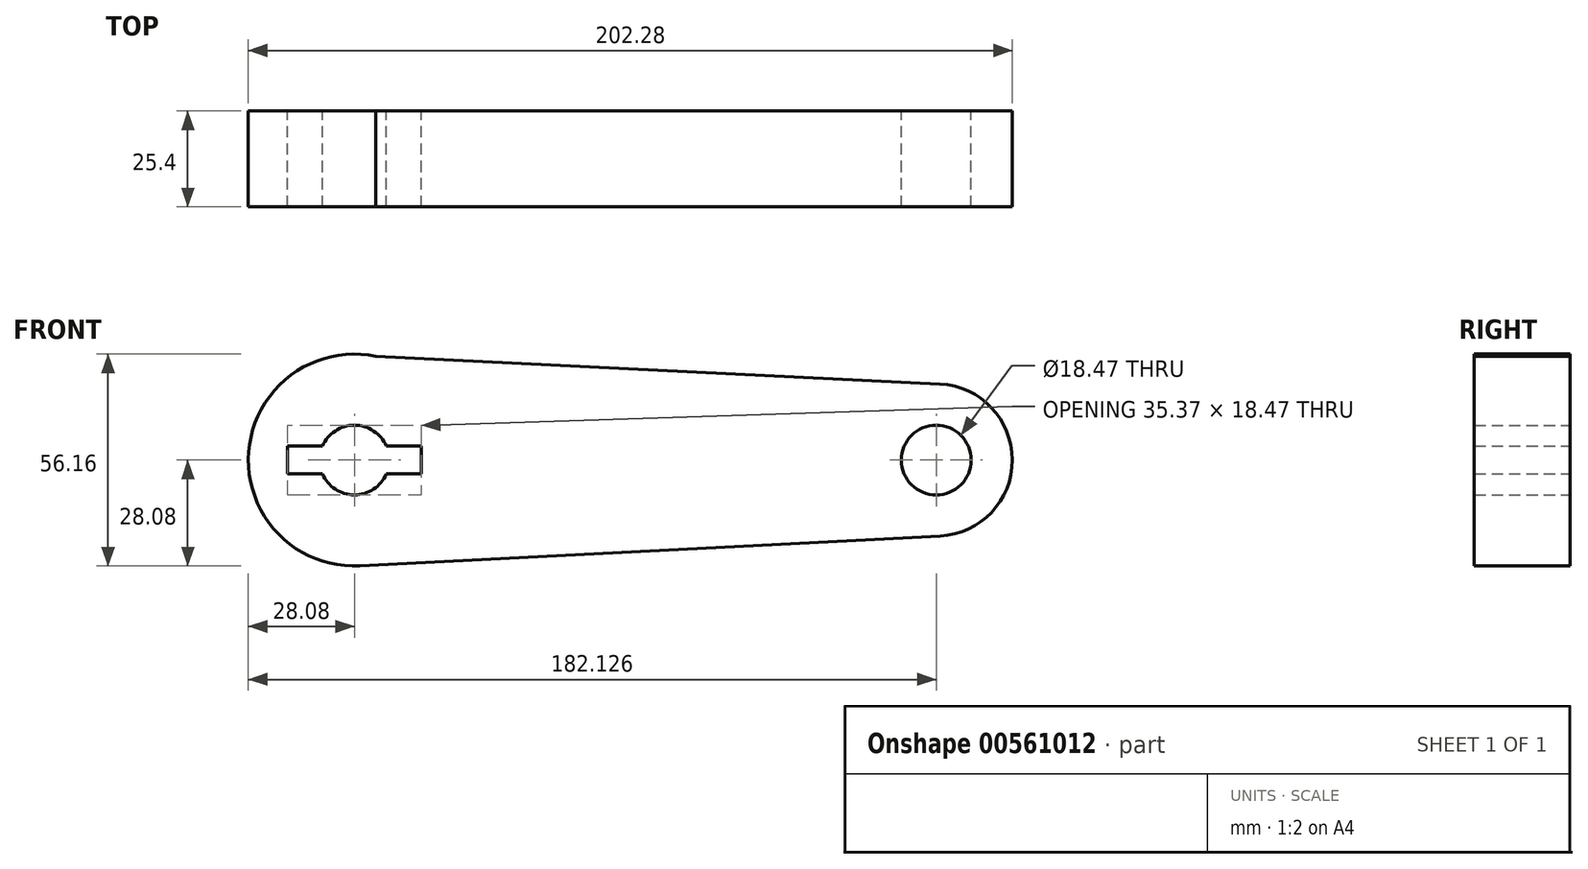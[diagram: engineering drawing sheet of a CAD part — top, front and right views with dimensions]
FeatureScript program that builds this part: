
annotation { "Feature Type Name" : "Feature", "Feature Type Description" : "" }
export const myFeature = defineFeature(function(context is Context, id is Id, definition is map)
    precondition{}
    {
        {
            var Q0;
            Q0=qCreatedBy(makeId("Front.planeOp"),FACE);
            var sketch = newSketch(context, id + "F0", { "sketchPlane" : qUnion([Q0])});
            skCircle(sketch, "E0", {"center": v(0, 0) * mm, "radius": 28.08 * mm});
            skCircle(sketch, "E1", {"center": v(154.05, 0) * mm, "radius": 20.15 * mm});
            skLineSegment(sketch, "E2", {"start": v(5.7, 27.49) * mm, "end": v(155.04, 20.13) * mm});
            skLineSegment(sketch, "E3", {"start": v(1.44, -28.04) * mm, "end": v(155.08, -20.13) * mm});
            skCircle(sketch, "E4", {"center": v(0, 0) * mm, "radius": 9.24 * mm});
            skCircle(sketch, "E5", {"center": v(154.05, 0) * mm, "radius": 9.24 * mm});
            skLineSegment(sketch, "E6.bottom", {"start": v(17.69, 3.68) * mm, "end": v(-17.69, 3.68) * mm});
            skLineSegment(sketch, "E6.top", {"start": v(17.69, -3.68) * mm, "end": v(-17.69, -3.68) * mm});
            skLineSegment(sketch, "E6.left", {"start": v(17.69, 3.68) * mm, "end": v(17.69, -3.68) * mm});
            skLineSegment(sketch, "E6.right", {"start": v(-17.69, 3.68) * mm, "end": v(-17.69, -3.68) * mm});
            skSolve(sketch);
        }
        {
            var Q0;
            Q0 = qSketchRegion(id + "F0", true);
            extrude(context, id + "F1", {"entities" : qUnion([Q0]), "depth" : 25.4 * mm, "offsetDistance" : 25.4 * mm});
        }
    });
